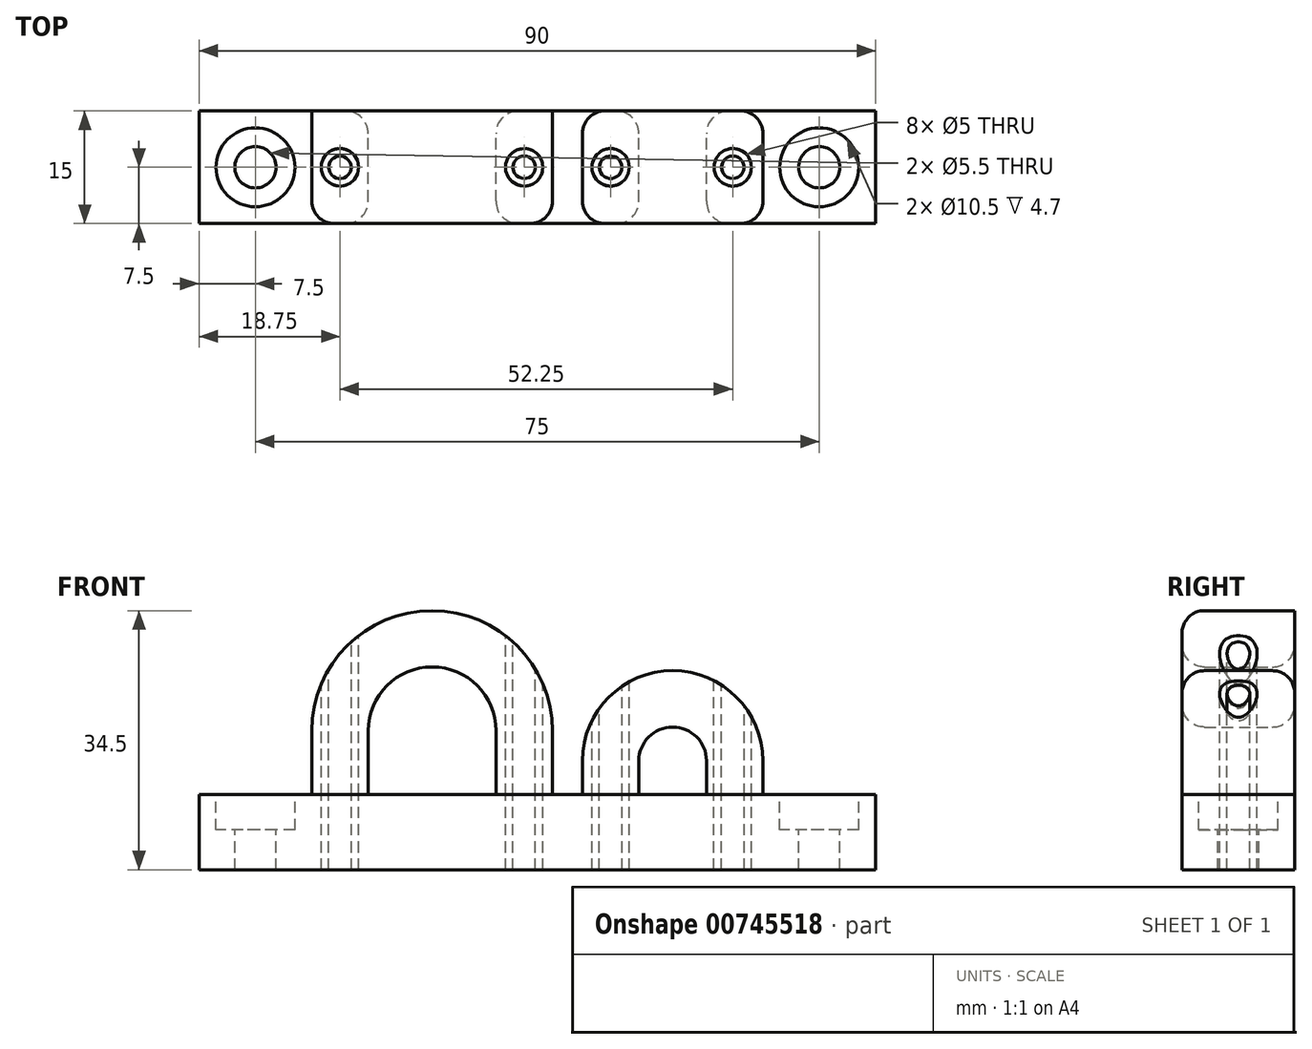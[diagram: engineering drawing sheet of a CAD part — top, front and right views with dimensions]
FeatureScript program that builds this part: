
annotation { "Feature Type Name" : "Feature", "Feature Type Description" : "" }
export const myFeature = defineFeature(function(context is Context, id is Id, definition is map)
    precondition{}
    {
        {
            var Q0;
            Q0=qCreatedBy(makeId("Front.planeOp"),FACE);
            var sketch = newSketch(context, id + "F0", { "sketchPlane" : qUnion([Q0])});
            skLineSegment(sketch, "E0", {"start": v(0, 0) * mm, "end": v(-34, 0) * mm});
            skLineSegment(sketch, "E1", {"start": v(-34, 0) * mm, "end": v(-34, 10) * mm});
            skLineSegment(sketch, "E2", {"start": v(-34, 10) * mm, "end": v(2.5, 10) * mm});
            skArc(sketch, "E3", {"start": v(-9.5, 18.5) * mm, "mid": v(-18, 27) * mm, "end": v(-26.5, 18.5) * mm});
            skArc(sketch, "E4.trimOffspring", {"start": v(-2, 18.5) * mm, "mid": v(-18, 34.5) * mm, "end": v(-34, 18.5) * mm});
            skLineSegment(sketch, "E5", {"start": v(-26.5, 18.5) * mm, "end": v(-26.5, 10) * mm});
            skLineSegment(sketch, "E6", {"start": v(-34, 18.5) * mm, "end": v(-34, 10) * mm});
            skLineSegment(sketch, "E7", {"start": v(-2, 18.5) * mm, "end": v(-2, 10) * mm});
            skLineSegment(sketch, "E8", {"start": v(-9.5, 18.5) * mm, "end": v(-9.5, 10) * mm});
            skLineSegment(sketch, "E9", {"start": v(0, 0) * mm, "end": v(26, 0) * mm});
            skLineSegment(sketch, "E10", {"start": v(2.5, 10) * mm, "end": v(26, 10) * mm});
            skLineSegment(sketch, "E11", {"start": v(26, 0) * mm, "end": v(26, 10) * mm});
            skArc(sketch, "E12", {"start": v(18.5, 14.5) * mm, "mid": v(14, 19) * mm, "end": v(9.5, 14.5) * mm});
            skArc(sketch, "E13", {"start": v(26, 14.5) * mm, "mid": v(14, 26.5) * mm, "end": v(2, 14.5) * mm});
            skLineSegment(sketch, "E14", {"start": v(9.5, 14.5) * mm, "end": v(8, 14.5) * mm});
            skLineSegment(sketch, "E15", {"start": v(18.5, 14.5) * mm, "end": v(20, 14.5) * mm});
            skLineSegment(sketch, "E16", {"start": v(26, 14.5) * mm, "end": v(26, 10) * mm});
            skLineSegment(sketch, "E17", {"start": v(2, 14.5) * mm, "end": v(2, 10) * mm});
            skLineSegment(sketch, "E18", {"start": v(18.5, 14.5) * mm, "end": v(18.5, 10) * mm});
            skLineSegment(sketch, "E19", {"start": v(9.5, 14.5) * mm, "end": v(9.5, 10) * mm});
            skLineSegment(sketch, "E20", {"start": v(-34, 0) * mm, "end": v(-49, 0) * mm});
            skLineSegment(sketch, "E21", {"start": v(-49, 0) * mm, "end": v(-49, 10) * mm});
            skLineSegment(sketch, "E22", {"start": v(-34, 10) * mm, "end": v(-49, 10) * mm});
            skLineSegment(sketch, "E23", {"start": v(26, 0) * mm, "end": v(41, 0) * mm});
            skLineSegment(sketch, "E24", {"start": v(41, 0) * mm, "end": v(41, 10) * mm});
            skLineSegment(sketch, "E25", {"start": v(26, 10) * mm, "end": v(41, 10) * mm});
            skSolve(sketch);
        }
        {
            var Q0;
            Q0=makeQuery(id+"F0.imprint","IMPRINT",FACE,{"disambiguationData":[TD([[makeQuery(id+"F0.imprint","IMPRINT",EDGE,{"derivedFrom":sQuery(id+"F0.wireOp",EDGE,"E1")}),1.0]])]});
            var Q1;
            Q1=makeQuery(id+"F0.imprint","IMPRINT",FACE,{"disambiguationData":[TD([[makeQuery(id+"F0.imprint","IMPRINT",EDGE,{"derivedFrom":sQuery(id+"F0.wireOp",EDGE,"E0")}),-1.0]])]});
            var Q2;
            Q2=makeQuery(id+"F0.imprint","IMPRINT",FACE,{"disambiguationData":[TD([[makeQuery(id+"F0.imprint","IMPRINT",EDGE,{"derivedFrom":sQuery(id+"F0.wireOp",EDGE,"E11")}),-1.0]])]});
            extrude(context, id + "F1", {"entities" : qUnion([Q0, Q1, Q2]), "endBound" : BoundingType.SYMMETRIC, "depth" : 15 * mm, "offsetDistance" : 25 * mm});
        }
        {
            var Q0;
            Q0=makeQuery(id+"F0.imprint","IMPRINT",FACE,{"disambiguationData":[TD([[makeQuery(id+"F0.imprint","IMPRINT",EDGE,{"derivedFrom":sQuery(id+"F0.wireOp",EDGE,"E3")}),-1.0]])]});
            var Q1;
            Q1=makeQuery(id+"F0.imprint","IMPRINT",FACE,{"disambiguationData":[TD([[makeQuery(id+"F0.imprint","IMPRINT",EDGE,{"derivedFrom":sQuery(id+"F0.wireOp",EDGE,"E12")}),-1.0]])]});
            extrude(context, id + "F2", {"entities" : qUnion([Q0, Q1]), "endBound" : BoundingType.SYMMETRIC, "depth" : 15 * mm, "offsetDistance" : 25 * mm});
        }
        {
            var Q0;
            Q0=qCreatedBy(makeId("Top.planeOp"),FACE);
            cPlane(context, id + "F3", {"entities" : qUnion([Q0]), "cplaneType" : CPlaneType.OFFSET, "offset" : 34.5 * mm, "width" : 150 * mm, "height" : 150 * mm});
        }
        {
            var Q0;
            Q0=qCreatedBy(id+"F3.planeOp",FACE);
            var sketch = newSketch(context, id + "F4", { "sketchPlane" : qUnion([Q0])});
            skLineSegment(sketch, "E26", {"start": v(0, 0) * mm, "end": v(-41.5, 0) * mm});
            skLineSegment(sketch, "E27", {"start": v(0, 0) * mm, "end": v(33.5, 0) * mm});
            skLineSegment(sketch, "E28", {"start": v(0, 0) * mm, "end": v(-5.75, 0) * mm});
            skLineSegment(sketch, "E29", {"start": v(0, 0) * mm, "end": v(-30.25, 0) * mm});
            skLineSegment(sketch, "E30", {"start": v(0, 0) * mm, "end": v(5.75, 0) * mm});
            skLineSegment(sketch, "E31", {"start": v(5.75, 0) * mm, "end": v(22, 0) * mm});
            skCircle(sketch, "E32", {"center": v(-30.25, 0) * mm, "radius": 1.5 * mm});
            skCircle(sketch, "E33", {"center": v(-30.25, 0) * mm, "radius": 2.5 * mm});
            skCircle(sketch, "E34", {"center": v(-5.75, 0) * mm, "radius": 1.5 * mm});
            skCircle(sketch, "E35", {"center": v(-5.75, 0) * mm, "radius": 2.5 * mm});
            skCircle(sketch, "E36", {"center": v(5.75, 0) * mm, "radius": 1.5 * mm});
            skCircle(sketch, "E37", {"center": v(5.75, 0) * mm, "radius": 2.5 * mm});
            skCircle(sketch, "E38", {"center": v(22, 0) * mm, "radius": 1.5 * mm});
            skCircle(sketch, "E39", {"center": v(22, 0) * mm, "radius": 2.5 * mm});
            skCircle(sketch, "E40", {"center": v(-41.5, 0) * mm, "radius": 2.75 * mm});
            skCircle(sketch, "E41", {"center": v(-41.5, 0) * mm, "radius": 5.25 * mm});
            skCircle(sketch, "E42", {"center": v(33.5, 0) * mm, "radius": 2.75 * mm});
            skCircle(sketch, "E43", {"center": v(33.5, 0) * mm, "radius": 5.25 * mm});
            skSolve(sketch);
        }
        {
            var Q0;
            {var subQ0=sQuery(id+"F4.wireOp",EDGE,"E29");var subQ1=sQuery(id+"F4.wireOp",EDGE,"E26");var subQ2=makeQuery(id+"F4.imprint","INTERSECT",VERTEX,{"derivedFrom":[subQ1,subQ0]});Q0=makeQuery(id+"F4.imprint","IMPRINT",FACE,{"disambiguationData":[TD([[makeQuery(id+"F4.imprint","IMPRINT",EDGE,{"disambiguationData":[TD([[subQ2,-1.0]])],"derivedFrom":subQ1}),-1.0]])]});}
            var Q1;
            {var subQ0=sQuery(id+"F4.wireOp",EDGE,"E29");var subQ1=sQuery(id+"F4.wireOp",EDGE,"E26");var subQ2=makeQuery(id+"F4.imprint","INTERSECT",VERTEX,{"derivedFrom":[subQ1,subQ0]});Q1=makeQuery(id+"F4.imprint","IMPRINT",FACE,{"disambiguationData":[TD([[makeQuery(id+"F4.imprint","IMPRINT",EDGE,{"disambiguationData":[TD([[subQ2,-1.0]])],"derivedFrom":subQ1}),1.0]])]});}
            var Q2;
            {var subQ0=sQuery(id+"F4.wireOp",EDGE,"E29");var subQ1=makeQuery(id+"F4.imprint","IMPRINT",VERTEX,{"derivedFrom":subQ0});Q2=makeQuery(id+"F4.imprint","IMPRINT",FACE,{"disambiguationData":[TD([[makeQuery(id+"F4.imprint","IMPRINT",EDGE,{"disambiguationData":[TD([[subQ1,1.0]])],"derivedFrom":subQ0}),-1.0]])]});}
            var Q3;
            {var subQ0=sQuery(id+"F4.wireOp",EDGE,"E29");var subQ1=makeQuery(id+"F4.imprint","IMPRINT",VERTEX,{"derivedFrom":subQ0});Q3=makeQuery(id+"F4.imprint","IMPRINT",FACE,{"disambiguationData":[TD([[makeQuery(id+"F4.imprint","IMPRINT",EDGE,{"disambiguationData":[TD([[subQ1,1.0]])],"derivedFrom":subQ0}),1.0]])]});}
            var Q4;
            {var subQ0=sQuery(id+"F4.wireOp",EDGE,"E31");var subQ1=sQuery(id+"F4.wireOp",EDGE,"E30");var subQ2=makeQuery(id+"F4.imprint","INTERSECT",VERTEX,{"derivedFrom":[subQ1,subQ0]});Q4=makeQuery(id+"F4.imprint","IMPRINT",FACE,{"disambiguationData":[TD([[makeQuery(id+"F4.imprint","IMPRINT",EDGE,{"disambiguationData":[TD([[subQ2,1.0]])],"derivedFrom":subQ1}),-1.0]])]});}
            var Q5;
            {var subQ0=sQuery(id+"F4.wireOp",EDGE,"E31");var subQ1=sQuery(id+"F4.wireOp",EDGE,"E30");var subQ2=makeQuery(id+"F4.imprint","INTERSECT",VERTEX,{"derivedFrom":[subQ1,subQ0]});Q5=makeQuery(id+"F4.imprint","IMPRINT",FACE,{"disambiguationData":[TD([[makeQuery(id+"F4.imprint","IMPRINT",EDGE,{"disambiguationData":[TD([[subQ2,1.0]])],"derivedFrom":subQ1}),1.0]])]});}
            var Q6;
            {var subQ0=sQuery(id+"F4.wireOp",EDGE,"E31");var subQ1=sQuery(id+"F4.wireOp",EDGE,"E27");var subQ2=makeQuery(id+"F4.imprint","INTERSECT",VERTEX,{"derivedFrom":[subQ1,subQ0]});Q6=makeQuery(id+"F4.imprint","IMPRINT",FACE,{"disambiguationData":[TD([[makeQuery(id+"F4.imprint","IMPRINT",EDGE,{"disambiguationData":[TD([[subQ2,-1.0]])],"derivedFrom":subQ1}),1.0]])]});}
            var Q7;
            {var subQ0=sQuery(id+"F4.wireOp",EDGE,"E31");var subQ1=sQuery(id+"F4.wireOp",EDGE,"E27");var subQ2=makeQuery(id+"F4.imprint","INTERSECT",VERTEX,{"derivedFrom":[subQ1,subQ0]});Q7=makeQuery(id+"F4.imprint","IMPRINT",FACE,{"disambiguationData":[TD([[makeQuery(id+"F4.imprint","IMPRINT",EDGE,{"disambiguationData":[TD([[subQ2,-1.0]])],"derivedFrom":subQ1}),-1.0]])]});}
            var Q8;
            Q8=makeQuery(id+"F4.imprint","IMPRINT",FACE,{"disambiguationData":[TD([[makeQuery(id+"F4.imprint","IMPRINT",EDGE,{"derivedFrom":sQuery(id+"F4.wireOp",EDGE,"E40")}),1.0]])]});
            var Q9;
            Q9=makeQuery(id+"F4.imprint","IMPRINT",FACE,{"disambiguationData":[TD([[makeQuery(id+"F4.imprint","IMPRINT",EDGE,{"derivedFrom":sQuery(id+"F4.wireOp",EDGE,"E42")}),1.0]])]});
            var Q10;
            Q10=sQuery(id+"F4.wireOp",EDGE,"E32");
            var Q11;
            Q11=sQuery(id+"F4.wireOp",EDGE,"E34");
            var Q12;
            Q12=sQuery(id+"F4.wireOp",EDGE,"E36");
            var Q13;
            Q13=sQuery(id+"F4.wireOp",EDGE,"E38");
            extrude(context, id + "F5", {"entities" : qUnion([Q0, Q1, Q2, Q3, Q4, Q5, Q6, Q7, Q8, Q9]), "operationType" : NewBodyOperationType.REMOVE, "surfaceEntities" : qUnion([Q10, Q11, Q12, Q13]), "oppositeDirection" : true, "depth" : 40 * mm, "offsetDistance" : 25 * mm});
        }
        {
            var Q0;
            {var subQ0=sQuery(id+"F4.wireOp",EDGE,"E33");var subQ1=sQuery(id+"F4.wireOp",EDGE,"E26");var subQ2=makeQuery(id+"F4.imprint","INTERSECT",VERTEX,{"derivedFrom":[subQ1,subQ0]});Q0=makeQuery(id+"F4.imprint","IMPRINT",FACE,{"disambiguationData":[TD([[makeQuery(id+"F4.imprint","IMPRINT",EDGE,{"disambiguationData":[TD([[subQ2,1.0]])],"derivedFrom":subQ1}),-1.0]])]});}
            var Q1;
            {var subQ0=sQuery(id+"F4.wireOp",EDGE,"E33");var subQ1=sQuery(id+"F4.wireOp",EDGE,"E26");var subQ2=makeQuery(id+"F4.imprint","INTERSECT",VERTEX,{"derivedFrom":[subQ1,subQ0]});Q1=makeQuery(id+"F4.imprint","IMPRINT",FACE,{"disambiguationData":[TD([[makeQuery(id+"F4.imprint","IMPRINT",EDGE,{"disambiguationData":[TD([[subQ2,1.0]])],"derivedFrom":subQ1}),1.0]])]});}
            var Q2;
            {var subQ0=sQuery(id+"F4.wireOp",EDGE,"E35");var subQ1=sQuery(id+"F4.wireOp",EDGE,"E29");var subQ2=makeQuery(id+"F4.imprint","INTERSECT",VERTEX,{"disambiguationData":[OD(0.0)],"derivedFrom":[subQ1,subQ0]});Q2=makeQuery(id+"F4.imprint","IMPRINT",FACE,{"disambiguationData":[TD([[makeQuery(id+"F4.imprint","IMPRINT",EDGE,{"disambiguationData":[TD([[subQ2,-1.0]])],"derivedFrom":subQ1}),-1.0]])]});}
            var Q3;
            {var subQ0=sQuery(id+"F4.wireOp",EDGE,"E35");var subQ1=sQuery(id+"F4.wireOp",EDGE,"E29");var subQ2=makeQuery(id+"F4.imprint","INTERSECT",VERTEX,{"disambiguationData":[OD(0.0)],"derivedFrom":[subQ1,subQ0]});Q3=makeQuery(id+"F4.imprint","IMPRINT",FACE,{"disambiguationData":[TD([[makeQuery(id+"F4.imprint","IMPRINT",EDGE,{"disambiguationData":[TD([[subQ2,-1.0]])],"derivedFrom":subQ1}),1.0]])]});}
            extrude(context, id + "F6", {"entities" : qUnion([Q0, Q1, Q2, Q3]), "operationType" : NewBodyOperationType.REMOVE, "oppositeDirection" : true, "depth" : 15 * mm, "offsetDistance" : 25 * mm});
        }
        {
            var Q0;
            {var subQ0=sQuery(id+"F4.wireOp",EDGE,"E37");var subQ1=sQuery(id+"F4.wireOp",EDGE,"E30");var subQ2=makeQuery(id+"F4.imprint","INTERSECT",VERTEX,{"derivedFrom":[subQ1,subQ0]});Q0=makeQuery(id+"F4.imprint","IMPRINT",FACE,{"disambiguationData":[TD([[makeQuery(id+"F4.imprint","IMPRINT",EDGE,{"disambiguationData":[TD([[subQ2,-1.0]])],"derivedFrom":subQ1}),1.0]])]});}
            var Q1;
            {var subQ0=sQuery(id+"F4.wireOp",EDGE,"E37");var subQ1=sQuery(id+"F4.wireOp",EDGE,"E30");var subQ2=makeQuery(id+"F4.imprint","INTERSECT",VERTEX,{"derivedFrom":[subQ1,subQ0]});Q1=makeQuery(id+"F4.imprint","IMPRINT",FACE,{"disambiguationData":[TD([[makeQuery(id+"F4.imprint","IMPRINT",EDGE,{"disambiguationData":[TD([[subQ2,-1.0]])],"derivedFrom":subQ1}),-1.0]])]});}
            var Q2;
            {var subQ0=sQuery(id+"F4.wireOp",EDGE,"E39");var subQ1=sQuery(id+"F4.wireOp",EDGE,"E27");var subQ2=makeQuery(id+"F4.imprint","INTERSECT",VERTEX,{"derivedFrom":[subQ1,subQ0]});Q2=makeQuery(id+"F4.imprint","IMPRINT",FACE,{"disambiguationData":[TD([[makeQuery(id+"F4.imprint","IMPRINT",EDGE,{"disambiguationData":[TD([[subQ2,1.0]])],"derivedFrom":subQ1}),1.0]])]});}
            var Q3;
            {var subQ0=sQuery(id+"F4.wireOp",EDGE,"E39");var subQ1=sQuery(id+"F4.wireOp",EDGE,"E27");var subQ2=makeQuery(id+"F4.imprint","INTERSECT",VERTEX,{"derivedFrom":[subQ1,subQ0]});Q3=makeQuery(id+"F4.imprint","IMPRINT",FACE,{"disambiguationData":[TD([[makeQuery(id+"F4.imprint","IMPRINT",EDGE,{"disambiguationData":[TD([[subQ2,1.0]])],"derivedFrom":subQ1}),-1.0]])]});}
            extrude(context, id + "F7", {"entities" : qUnion([Q0, Q1, Q2, Q3]), "operationType" : NewBodyOperationType.REMOVE, "oppositeDirection" : true, "depth" : 18 * mm, "offsetDistance" : 25 * mm});
        }
        {
            var Q0;
            Q0=makeQuery(id+"F4.imprint","IMPRINT",FACE,{"disambiguationData":[TD([[makeQuery(id+"F4.imprint","IMPRINT",EDGE,{"derivedFrom":sQuery(id+"F4.wireOp",EDGE,"E40")}),-1.0]])]});
            var Q1;
            Q1=makeQuery(id+"F4.imprint","IMPRINT",FACE,{"disambiguationData":[TD([[makeQuery(id+"F4.imprint","IMPRINT",EDGE,{"derivedFrom":sQuery(id+"F4.wireOp",EDGE,"E42")}),-1.0]])]});
            extrude(context, id + "F8", {"entities" : qUnion([Q0, Q1]), "operationType" : NewBodyOperationType.REMOVE, "oppositeDirection" : true, "depth" : 29.2 * mm, "offsetDistance" : 25 * mm});
        }
        {
            var Q0;
            Q0=makeQuery(id+"F2.opExtrude","CAP_EDGE",EDGE,{"disambiguationData":[OSD([sQuery(id+"F0.wireOp",EDGE,"E4.trimOffspring")])],"isStart":false});
            var Q1;
            Q1=makeQuery(id+"F2.opExtrude","CAP_EDGE",EDGE,{"disambiguationData":[OSD([sQuery(id+"F0.wireOp",EDGE,"E3")])],"isStart":false});
            var Q2;
            Q2=makeQuery(id+"F2.opExtrude","CAP_EDGE",EDGE,{"disambiguationData":[OSD([sQuery(id+"F0.wireOp",EDGE,"E13")])],"isStart":false});
            var Q3;
            Q3=makeQuery(id+"F2.opExtrude","CAP_EDGE",EDGE,{"disambiguationData":[OSD([sQuery(id+"F0.wireOp",EDGE,"E12")])],"isStart":false});
            var Q4;
            Q4=makeQuery(id+"F2.opExtrude","CAP_EDGE",EDGE,{"disambiguationData":[OSD([sQuery(id+"F0.wireOp",EDGE,"E12")])],"isStart":true});
            var Q5;
            Q5=makeQuery(id+"F2.opExtrude","CAP_EDGE",EDGE,{"disambiguationData":[OSD([sQuery(id+"F0.wireOp",EDGE,"E3")])],"isStart":true});
            var Q6;
            Q6=makeQuery(id+"F2.opExtrude","CAP_EDGE",EDGE,{"disambiguationData":[OSD([sQuery(id+"F0.wireOp",EDGE,"E13")])],"isStart":true});
            fillet(context, id + "F9", {"entities" : qUnion([Q0, Q1, Q2, Q3, Q4, Q5, Q6]), "radius" : 3 * mm, "tangentPropagation" : true, "allowEdgeOverflow" : false});
        }
    });
